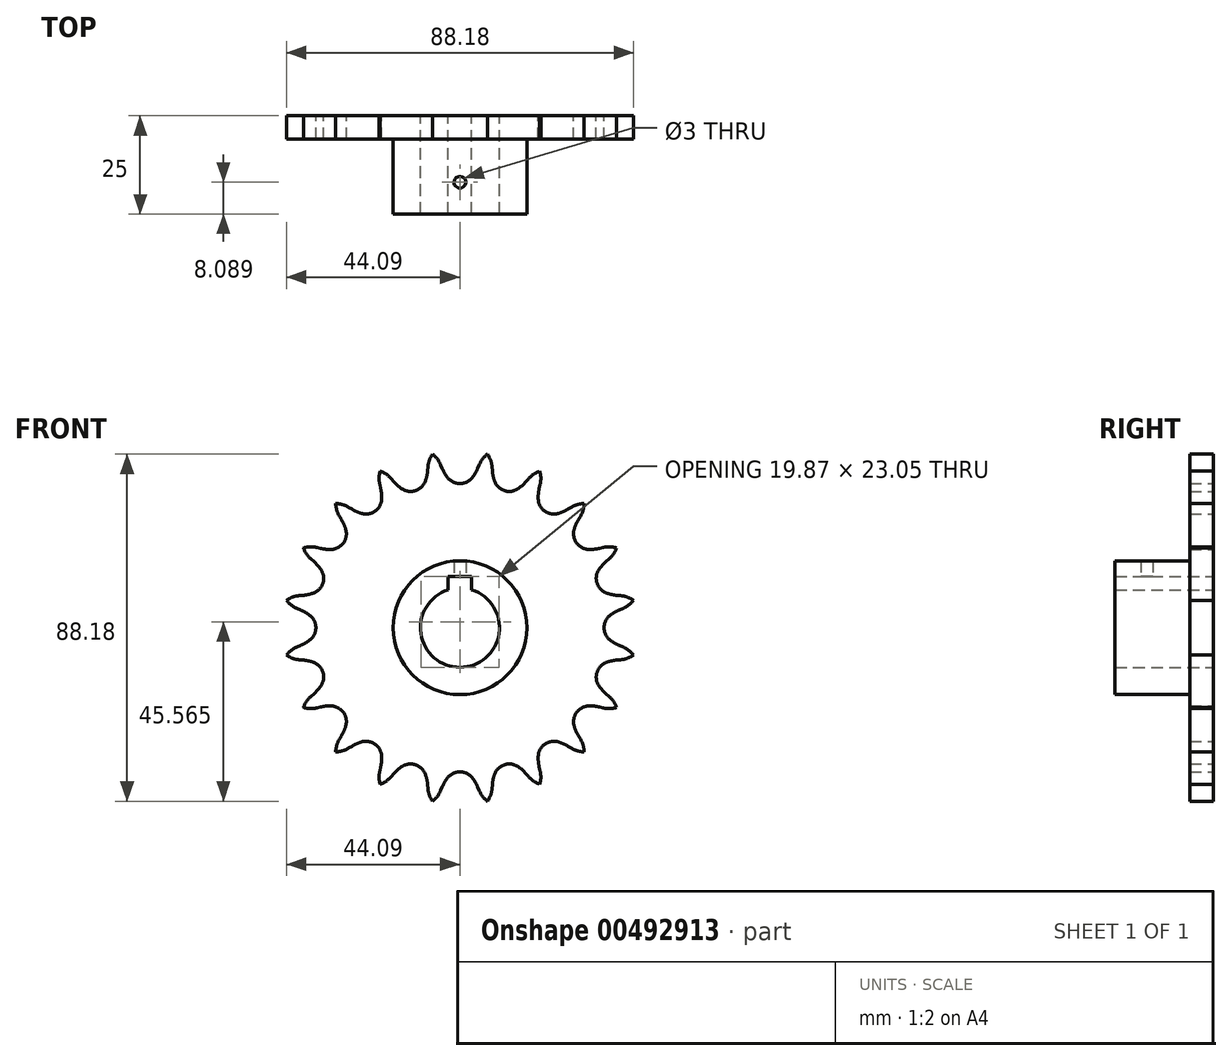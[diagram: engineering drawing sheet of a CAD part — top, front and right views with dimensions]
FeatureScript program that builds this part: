
annotation { "Feature Type Name" : "Feature", "Feature Type Description" : "" }
export const myFeature = defineFeature(function(context is Context, id is Id, definition is map)
    precondition{}
    {
        {
            var Q0;
            Q0=qCreatedBy(makeId("Front.planeOp"),FACE);
            var sketch = newSketch(context, id + "F0", { "sketchPlane" : qUnion([Q0])});
            skCircle(sketch, "E0", {"center": v(0, 0) * mm, "radius": 40.6 * mm, "construction": true});
            skLineSegment(sketch, "E1", {"start": v(0, 0) * mm, "end": v(0, 68.21) * mm, "construction": true});
            skLineSegment(sketch, "E2", {"start": v(-42.58, 40.6) * mm, "end": v(46.68, 40.6) * mm, "construction": true});
            skArc(sketch, "E3", {"start": v(-3.14, 38.14) * mm, "mid": v(-1.75, 37.01) * mm, "end": v(0, 36.61) * mm});
            skLineSegment(sketch, "E4.0", {"start": v(5, 0) * mm, "end": v(5, 68.21) * mm, "construction": true});
            skLineSegment(sketch, "E5.0", {"start": v(-42.58, 44.5) * mm, "end": v(46.68, 44.5) * mm, "construction": true});
            skLineSegment(sketch, "E6", {"start": v(-5.48, 36.31) * mm, "end": v(8.35, 47.12) * mm, "construction": true});
            skLineSegment(sketch, "E7", {"start": v(5, 44.5) * mm, "end": v(-4.52, 40.5) * mm, "construction": true});
            skArc(sketch, "E8", {"start": v(-4.52, 40.5) * mm, "mid": v(-3.9, 39.27) * mm, "end": v(-3.14, 38.14) * mm});
            skLineSegment(sketch, "E9", {"start": v(-4.52, 40.5) * mm, "end": v(-4.9, 41.4) * mm});
            skLineSegment(sketch, "E10.0", {"start": v(-10.95, 0) * mm, "end": v(-10.95, 68.21) * mm, "construction": true});
            skLineSegment(sketch, "E11.0", {"start": v(-42.58, 38.86) * mm, "end": v(46.68, 38.86) * mm, "construction": true});
            skLineSegment(sketch, "E12", {"start": v(0, 0) * mm, "end": v(-9.3, 58.75) * mm, "construction": true});
            skArc(sketch, "E13.trimOffspring", {"start": v(-4.89, 41.37) * mm, "mid": v(-5.75, 42.87) * mm, "end": v(-6.98, 44.09) * mm});
            skArc(sketch, "E14.trimOffspring", {"start": v(3.98, 40.4) * mm, "mid": v(3.98, 40.5) * mm, "end": v(3.98, 40.6) * mm});
            skArc(sketch, "E15.MirrorCS", {"start": v(4.89, 41.37) * mm, "mid": v(5.75, 42.87) * mm, "end": v(6.98, 44.09) * mm});
            skLineSegment(sketch, "E16.MirrorCS", {"start": v(4.52, 40.5) * mm, "end": v(4.9, 41.4) * mm});
            skArc(sketch, "E17.MirrorCS", {"start": v(4.52, 40.5) * mm, "mid": v(3.9, 39.27) * mm, "end": v(3.14, 38.14) * mm});
            skArc(sketch, "E18.MirrorCS", {"start": v(3.14, 38.14) * mm, "mid": v(1.75, 37.01) * mm, "end": v(0, 36.61) * mm});
            skArc(sketch, "E19.1.0", {"start": v(-17.43, 37.84) * mm, "mid": v(-18.72, 39) * mm, "end": v(-20.26, 39.77) * mm});
            skLineSegment(sketch, "E19.1.1", {"start": v(-16.81, 37.12) * mm, "end": v(-17.45, 37.86) * mm});
            skArc(sketch, "E19.1.2", {"start": v(-16.81, 37.12) * mm, "mid": v(-15.85, 36.14) * mm, "end": v(-14.77, 35.3) * mm});
            skArc(sketch, "E19.1.3", {"start": v(-14.77, 35.3) * mm, "mid": v(-13.1, 34.66) * mm, "end": v(-11.31, 34.82) * mm});
            skArc(sketch, "E19.1.4", {"start": v(-8.8, 37.24) * mm, "mid": v(-9.78, 35.74) * mm, "end": v(-11.31, 34.82) * mm});
            skArc(sketch, "E19.1.5", {"start": v(-8.22, 39.9) * mm, "mid": v(-8.42, 38.56) * mm, "end": v(-8.8, 37.24) * mm});
            skLineSegment(sketch, "E19.1.6", {"start": v(-8.22, 39.9) * mm, "end": v(-8.13, 40.89) * mm});
            skArc(sketch, "E19.1.7", {"start": v(-8.14, 40.86) * mm, "mid": v(-7.77, 42.55) * mm, "end": v(-6.98, 44.09) * mm});
            skArc(sketch, "E19.2.0", {"start": v(-28.27, 30.6) * mm, "mid": v(-29.85, 31.3) * mm, "end": v(-31.56, 31.56) * mm});
            skLineSegment(sketch, "E19.2.1", {"start": v(-27.46, 30.1) * mm, "end": v(-28.3, 30.61) * mm});
            skArc(sketch, "E19.2.2", {"start": v(-27.46, 30.1) * mm, "mid": v(-26.24, 29.48) * mm, "end": v(-24.96, 29.01) * mm});
            skArc(sketch, "E19.2.3", {"start": v(-24.96, 29.01) * mm, "mid": v(-23.17, 28.92) * mm, "end": v(-21.52, 29.62) * mm});
            skArc(sketch, "E19.2.4", {"start": v(-19.88, 32.7) * mm, "mid": v(-20.34, 30.97) * mm, "end": v(-21.52, 29.62) * mm});
            skArc(sketch, "E19.2.5", {"start": v(-20.15, 35.42) * mm, "mid": v(-19.92, 34.07) * mm, "end": v(-19.88, 32.7) * mm});
            skLineSegment(sketch, "E19.2.6", {"start": v(-20.15, 35.42) * mm, "end": v(-20.37, 36.37) * mm});
            skArc(sketch, "E19.2.7", {"start": v(-20.36, 36.34) * mm, "mid": v(-20.54, 38.06) * mm, "end": v(-20.26, 39.77) * mm});
            skArc(sketch, "E20.1.3.0", {"start": v(-36.34, 20.36) * mm, "mid": v(-38.06, 20.54) * mm, "end": v(-39.77, 20.26) * mm});
            skLineSegment(sketch, "E20.4.3.0", {"start": v(-35.42, 20.15) * mm, "end": v(-36.37, 20.37) * mm});
            skArc(sketch, "E20.7.3.0", {"start": v(-35.42, 20.15) * mm, "mid": v(-34.07, 19.92) * mm, "end": v(-32.7, 19.88) * mm});
            skArc(sketch, "E20.11.3.0", {"start": v(-32.7, 19.88) * mm, "mid": v(-30.97, 20.34) * mm, "end": v(-29.62, 21.52) * mm});
            skArc(sketch, "E20.15.3.0", {"start": v(-29.01, 24.96) * mm, "mid": v(-28.92, 23.17) * mm, "end": v(-29.62, 21.52) * mm});
            skArc(sketch, "E20.19.3.0", {"start": v(-30.1, 27.46) * mm, "mid": v(-29.48, 26.24) * mm, "end": v(-29.01, 24.96) * mm});
            skLineSegment(sketch, "E20.23.3.0", {"start": v(-30.1, 27.46) * mm, "end": v(-30.61, 28.3) * mm});
            skArc(sketch, "E20.26.3.0", {"start": v(-30.6, 28.27) * mm, "mid": v(-31.3, 29.85) * mm, "end": v(-31.56, 31.56) * mm});
            skArc(sketch, "E20.1.4.0", {"start": v(-40.86, 8.14) * mm, "mid": v(-42.55, 7.77) * mm, "end": v(-44.09, 6.98) * mm});
            skLineSegment(sketch, "E20.4.4.0", {"start": v(-39.9, 8.22) * mm, "end": v(-40.89, 8.13) * mm});
            skArc(sketch, "E20.7.4.0", {"start": v(-39.9, 8.22) * mm, "mid": v(-38.56, 8.42) * mm, "end": v(-37.24, 8.8) * mm});
            skArc(sketch, "E20.11.4.0", {"start": v(-37.24, 8.8) * mm, "mid": v(-35.74, 9.78) * mm, "end": v(-34.82, 11.31) * mm});
            skArc(sketch, "E20.15.4.0", {"start": v(-35.3, 14.77) * mm, "mid": v(-34.66, 13.1) * mm, "end": v(-34.82, 11.31) * mm});
            skArc(sketch, "E20.19.4.0", {"start": v(-37.12, 16.81) * mm, "mid": v(-36.14, 15.85) * mm, "end": v(-35.3, 14.77) * mm});
            skLineSegment(sketch, "E20.23.4.0", {"start": v(-37.12, 16.81) * mm, "end": v(-37.86, 17.45) * mm});
            skArc(sketch, "E20.26.4.0", {"start": v(-37.84, 17.43) * mm, "mid": v(-39, 18.72) * mm, "end": v(-39.77, 20.26) * mm});
            skArc(sketch, "E20.1.5.0", {"start": v(-41.37, -4.89) * mm, "mid": v(-42.87, -5.75) * mm, "end": v(-44.09, -6.98) * mm});
            skLineSegment(sketch, "E20.4.5.0", {"start": v(-40.5, -4.52) * mm, "end": v(-41.4, -4.9) * mm});
            skArc(sketch, "E20.7.5.0", {"start": v(-40.5, -4.52) * mm, "mid": v(-39.27, -3.9) * mm, "end": v(-38.14, -3.14) * mm});
            skArc(sketch, "E20.11.5.0", {"start": v(-38.14, -3.14) * mm, "mid": v(-37.01, -1.75) * mm, "end": v(-36.61, 0) * mm});
            skArc(sketch, "E20.15.5.0", {"start": v(-38.14, 3.14) * mm, "mid": v(-37.01, 1.75) * mm, "end": v(-36.61, 0) * mm});
            skArc(sketch, "E20.19.5.0", {"start": v(-40.5, 4.52) * mm, "mid": v(-39.27, 3.9) * mm, "end": v(-38.14, 3.14) * mm});
            skLineSegment(sketch, "E20.23.5.0", {"start": v(-40.5, 4.52) * mm, "end": v(-41.4, 4.9) * mm});
            skArc(sketch, "E20.26.5.0", {"start": v(-41.37, 4.89) * mm, "mid": v(-42.87, 5.75) * mm, "end": v(-44.09, 6.98) * mm});
            skArc(sketch, "E20.1.6.0", {"start": v(-37.84, -17.43) * mm, "mid": v(-39, -18.72) * mm, "end": v(-39.77, -20.26) * mm});
            skLineSegment(sketch, "E20.4.6.0", {"start": v(-37.12, -16.81) * mm, "end": v(-37.86, -17.45) * mm});
            skArc(sketch, "E20.7.6.0", {"start": v(-37.12, -16.81) * mm, "mid": v(-36.14, -15.85) * mm, "end": v(-35.3, -14.77) * mm});
            skArc(sketch, "E20.11.6.0", {"start": v(-35.3, -14.77) * mm, "mid": v(-34.66, -13.1) * mm, "end": v(-34.82, -11.31) * mm});
            skArc(sketch, "E20.15.6.0", {"start": v(-37.24, -8.8) * mm, "mid": v(-35.74, -9.78) * mm, "end": v(-34.82, -11.31) * mm});
            skArc(sketch, "E20.19.6.0", {"start": v(-39.9, -8.22) * mm, "mid": v(-38.56, -8.42) * mm, "end": v(-37.24, -8.8) * mm});
            skLineSegment(sketch, "E20.23.6.0", {"start": v(-39.9, -8.22) * mm, "end": v(-40.89, -8.13) * mm});
            skArc(sketch, "E20.26.6.0", {"start": v(-40.86, -8.14) * mm, "mid": v(-42.55, -7.77) * mm, "end": v(-44.09, -6.98) * mm});
            skArc(sketch, "E20.1.7.0", {"start": v(-30.6, -28.27) * mm, "mid": v(-31.3, -29.85) * mm, "end": v(-31.56, -31.56) * mm});
            skLineSegment(sketch, "E20.4.7.0", {"start": v(-30.1, -27.46) * mm, "end": v(-30.61, -28.3) * mm});
            skArc(sketch, "E20.7.7.0", {"start": v(-30.1, -27.46) * mm, "mid": v(-29.48, -26.24) * mm, "end": v(-29.01, -24.96) * mm});
            skArc(sketch, "E20.11.7.0", {"start": v(-29.01, -24.96) * mm, "mid": v(-28.92, -23.17) * mm, "end": v(-29.62, -21.52) * mm});
            skArc(sketch, "E20.15.7.0", {"start": v(-32.7, -19.88) * mm, "mid": v(-30.97, -20.34) * mm, "end": v(-29.62, -21.52) * mm});
            skArc(sketch, "E20.19.7.0", {"start": v(-35.42, -20.15) * mm, "mid": v(-34.07, -19.92) * mm, "end": v(-32.7, -19.88) * mm});
            skLineSegment(sketch, "E20.23.7.0", {"start": v(-35.42, -20.15) * mm, "end": v(-36.37, -20.37) * mm});
            skArc(sketch, "E20.26.7.0", {"start": v(-36.34, -20.36) * mm, "mid": v(-38.06, -20.54) * mm, "end": v(-39.77, -20.26) * mm});
            skArc(sketch, "E20.1.8.0", {"start": v(-20.36, -36.34) * mm, "mid": v(-20.54, -38.06) * mm, "end": v(-20.26, -39.77) * mm});
            skLineSegment(sketch, "E20.4.8.0", {"start": v(-20.15, -35.42) * mm, "end": v(-20.37, -36.37) * mm});
            skArc(sketch, "E20.7.8.0", {"start": v(-20.15, -35.42) * mm, "mid": v(-19.92, -34.07) * mm, "end": v(-19.88, -32.7) * mm});
            skArc(sketch, "E20.11.8.0", {"start": v(-19.88, -32.7) * mm, "mid": v(-20.34, -30.97) * mm, "end": v(-21.52, -29.62) * mm});
            skArc(sketch, "E20.15.8.0", {"start": v(-24.96, -29.01) * mm, "mid": v(-23.17, -28.92) * mm, "end": v(-21.52, -29.62) * mm});
            skArc(sketch, "E20.19.8.0", {"start": v(-27.46, -30.1) * mm, "mid": v(-26.24, -29.48) * mm, "end": v(-24.96, -29.01) * mm});
            skLineSegment(sketch, "E20.23.8.0", {"start": v(-27.46, -30.1) * mm, "end": v(-28.3, -30.61) * mm});
            skArc(sketch, "E20.26.8.0", {"start": v(-28.27, -30.6) * mm, "mid": v(-29.85, -31.3) * mm, "end": v(-31.56, -31.56) * mm});
            skArc(sketch, "E20.1.9.0", {"start": v(-8.14, -40.86) * mm, "mid": v(-7.77, -42.55) * mm, "end": v(-6.98, -44.09) * mm});
            skLineSegment(sketch, "E20.4.9.0", {"start": v(-8.22, -39.9) * mm, "end": v(-8.13, -40.89) * mm});
            skArc(sketch, "E20.7.9.0", {"start": v(-8.22, -39.9) * mm, "mid": v(-8.42, -38.56) * mm, "end": v(-8.8, -37.24) * mm});
            skArc(sketch, "E20.11.9.0", {"start": v(-8.8, -37.24) * mm, "mid": v(-9.78, -35.74) * mm, "end": v(-11.31, -34.82) * mm});
            skArc(sketch, "E20.15.9.0", {"start": v(-14.77, -35.3) * mm, "mid": v(-13.1, -34.66) * mm, "end": v(-11.31, -34.82) * mm});
            skArc(sketch, "E20.19.9.0", {"start": v(-16.81, -37.12) * mm, "mid": v(-15.85, -36.14) * mm, "end": v(-14.77, -35.3) * mm});
            skLineSegment(sketch, "E20.23.9.0", {"start": v(-16.81, -37.12) * mm, "end": v(-17.45, -37.86) * mm});
            skArc(sketch, "E20.26.9.0", {"start": v(-17.43, -37.84) * mm, "mid": v(-18.72, -39) * mm, "end": v(-20.26, -39.77) * mm});
            skArc(sketch, "E20.1.10.0", {"start": v(4.89, -41.37) * mm, "mid": v(5.75, -42.87) * mm, "end": v(6.98, -44.09) * mm});
            skLineSegment(sketch, "E20.4.10.0", {"start": v(4.52, -40.5) * mm, "end": v(4.9, -41.4) * mm});
            skArc(sketch, "E20.7.10.0", {"start": v(4.52, -40.5) * mm, "mid": v(3.9, -39.27) * mm, "end": v(3.14, -38.14) * mm});
            skArc(sketch, "E20.11.10.0", {"start": v(3.14, -38.14) * mm, "mid": v(1.75, -37.01) * mm, "end": v(0, -36.61) * mm});
            skArc(sketch, "E20.15.10.0", {"start": v(-3.14, -38.14) * mm, "mid": v(-1.75, -37.01) * mm, "end": v(0, -36.61) * mm});
            skArc(sketch, "E20.19.10.0", {"start": v(-4.52, -40.5) * mm, "mid": v(-3.9, -39.27) * mm, "end": v(-3.14, -38.14) * mm});
            skLineSegment(sketch, "E20.23.10.0", {"start": v(-4.52, -40.5) * mm, "end": v(-4.9, -41.4) * mm});
            skArc(sketch, "E20.26.10.0", {"start": v(-4.89, -41.37) * mm, "mid": v(-5.75, -42.87) * mm, "end": v(-6.98, -44.09) * mm});
            skArc(sketch, "E20.1.11.0", {"start": v(17.43, -37.84) * mm, "mid": v(18.72, -39) * mm, "end": v(20.26, -39.77) * mm});
            skLineSegment(sketch, "E20.4.11.0", {"start": v(16.81, -37.12) * mm, "end": v(17.45, -37.86) * mm});
            skArc(sketch, "E20.7.11.0", {"start": v(16.81, -37.12) * mm, "mid": v(15.85, -36.14) * mm, "end": v(14.77, -35.3) * mm});
            skArc(sketch, "E20.11.11.0", {"start": v(14.77, -35.3) * mm, "mid": v(13.1, -34.66) * mm, "end": v(11.31, -34.82) * mm});
            skArc(sketch, "E20.15.11.0", {"start": v(8.8, -37.24) * mm, "mid": v(9.78, -35.74) * mm, "end": v(11.31, -34.82) * mm});
            skArc(sketch, "E20.19.11.0", {"start": v(8.22, -39.9) * mm, "mid": v(8.42, -38.56) * mm, "end": v(8.8, -37.24) * mm});
            skLineSegment(sketch, "E20.23.11.0", {"start": v(8.22, -39.9) * mm, "end": v(8.13, -40.89) * mm});
            skArc(sketch, "E20.26.11.0", {"start": v(8.14, -40.86) * mm, "mid": v(7.77, -42.55) * mm, "end": v(6.98, -44.09) * mm});
            skArc(sketch, "E20.1.12.0", {"start": v(28.27, -30.6) * mm, "mid": v(29.85, -31.3) * mm, "end": v(31.56, -31.56) * mm});
            skLineSegment(sketch, "E20.4.12.0", {"start": v(27.46, -30.1) * mm, "end": v(28.3, -30.61) * mm});
            skArc(sketch, "E20.7.12.0", {"start": v(27.46, -30.1) * mm, "mid": v(26.24, -29.48) * mm, "end": v(24.96, -29.01) * mm});
            skArc(sketch, "E20.11.12.0", {"start": v(24.96, -29.01) * mm, "mid": v(23.17, -28.92) * mm, "end": v(21.52, -29.62) * mm});
            skArc(sketch, "E20.15.12.0", {"start": v(19.88, -32.7) * mm, "mid": v(20.34, -30.97) * mm, "end": v(21.52, -29.62) * mm});
            skArc(sketch, "E20.19.12.0", {"start": v(20.15, -35.42) * mm, "mid": v(19.92, -34.07) * mm, "end": v(19.88, -32.7) * mm});
            skLineSegment(sketch, "E20.23.12.0", {"start": v(20.15, -35.42) * mm, "end": v(20.37, -36.37) * mm});
            skArc(sketch, "E20.26.12.0", {"start": v(20.36, -36.34) * mm, "mid": v(20.54, -38.06) * mm, "end": v(20.26, -39.77) * mm});
            skArc(sketch, "E20.1.13.0", {"start": v(36.34, -20.36) * mm, "mid": v(38.06, -20.54) * mm, "end": v(39.77, -20.26) * mm});
            skLineSegment(sketch, "E20.4.13.0", {"start": v(35.42, -20.15) * mm, "end": v(36.37, -20.37) * mm});
            skArc(sketch, "E20.7.13.0", {"start": v(35.42, -20.15) * mm, "mid": v(34.07, -19.92) * mm, "end": v(32.7, -19.88) * mm});
            skArc(sketch, "E20.11.13.0", {"start": v(32.7, -19.88) * mm, "mid": v(30.97, -20.34) * mm, "end": v(29.62, -21.52) * mm});
            skArc(sketch, "E20.15.13.0", {"start": v(29.01, -24.96) * mm, "mid": v(28.92, -23.17) * mm, "end": v(29.62, -21.52) * mm});
            skArc(sketch, "E20.19.13.0", {"start": v(30.1, -27.46) * mm, "mid": v(29.48, -26.24) * mm, "end": v(29.01, -24.96) * mm});
            skLineSegment(sketch, "E20.23.13.0", {"start": v(30.1, -27.46) * mm, "end": v(30.61, -28.3) * mm});
            skArc(sketch, "E20.26.13.0", {"start": v(30.6, -28.27) * mm, "mid": v(31.3, -29.85) * mm, "end": v(31.56, -31.56) * mm});
            skArc(sketch, "E20.1.14.0", {"start": v(40.86, -8.14) * mm, "mid": v(42.55, -7.77) * mm, "end": v(44.09, -6.98) * mm});
            skLineSegment(sketch, "E20.4.14.0", {"start": v(39.9, -8.22) * mm, "end": v(40.89, -8.13) * mm});
            skArc(sketch, "E20.7.14.0", {"start": v(39.9, -8.22) * mm, "mid": v(38.56, -8.42) * mm, "end": v(37.24, -8.8) * mm});
            skArc(sketch, "E20.11.14.0", {"start": v(37.24, -8.8) * mm, "mid": v(35.74, -9.78) * mm, "end": v(34.82, -11.31) * mm});
            skArc(sketch, "E20.15.14.0", {"start": v(35.3, -14.77) * mm, "mid": v(34.66, -13.1) * mm, "end": v(34.82, -11.31) * mm});
            skArc(sketch, "E20.19.14.0", {"start": v(37.12, -16.81) * mm, "mid": v(36.14, -15.85) * mm, "end": v(35.3, -14.77) * mm});
            skLineSegment(sketch, "E20.23.14.0", {"start": v(37.12, -16.81) * mm, "end": v(37.86, -17.45) * mm});
            skArc(sketch, "E20.26.14.0", {"start": v(37.84, -17.43) * mm, "mid": v(39, -18.72) * mm, "end": v(39.77, -20.26) * mm});
            skArc(sketch, "E20.1.15.0", {"start": v(41.37, 4.89) * mm, "mid": v(42.87, 5.75) * mm, "end": v(44.09, 6.98) * mm});
            skLineSegment(sketch, "E20.4.15.0", {"start": v(40.5, 4.52) * mm, "end": v(41.4, 4.9) * mm});
            skArc(sketch, "E20.7.15.0", {"start": v(40.5, 4.52) * mm, "mid": v(39.27, 3.9) * mm, "end": v(38.14, 3.14) * mm});
            skArc(sketch, "E20.11.15.0", {"start": v(38.14, 3.14) * mm, "mid": v(37.01, 1.75) * mm, "end": v(36.61, 0) * mm});
            skArc(sketch, "E20.15.15.0", {"start": v(38.14, -3.14) * mm, "mid": v(37.01, -1.75) * mm, "end": v(36.61, 0) * mm});
            skArc(sketch, "E20.19.15.0", {"start": v(40.5, -4.52) * mm, "mid": v(39.27, -3.9) * mm, "end": v(38.14, -3.14) * mm});
            skLineSegment(sketch, "E20.23.15.0", {"start": v(40.5, -4.52) * mm, "end": v(41.4, -4.9) * mm});
            skArc(sketch, "E20.26.15.0", {"start": v(41.37, -4.89) * mm, "mid": v(42.87, -5.75) * mm, "end": v(44.09, -6.98) * mm});
            skArc(sketch, "E20.1.16.0", {"start": v(37.84, 17.43) * mm, "mid": v(39, 18.72) * mm, "end": v(39.77, 20.26) * mm});
            skLineSegment(sketch, "E20.4.16.0", {"start": v(37.12, 16.81) * mm, "end": v(37.86, 17.45) * mm});
            skArc(sketch, "E20.7.16.0", {"start": v(37.12, 16.81) * mm, "mid": v(36.14, 15.85) * mm, "end": v(35.3, 14.77) * mm});
            skArc(sketch, "E20.11.16.0", {"start": v(35.3, 14.77) * mm, "mid": v(34.66, 13.1) * mm, "end": v(34.82, 11.31) * mm});
            skArc(sketch, "E20.15.16.0", {"start": v(37.24, 8.8) * mm, "mid": v(35.74, 9.78) * mm, "end": v(34.82, 11.31) * mm});
            skArc(sketch, "E20.19.16.0", {"start": v(39.9, 8.22) * mm, "mid": v(38.56, 8.42) * mm, "end": v(37.24, 8.8) * mm});
            skLineSegment(sketch, "E20.23.16.0", {"start": v(39.9, 8.22) * mm, "end": v(40.89, 8.13) * mm});
            skArc(sketch, "E20.26.16.0", {"start": v(40.86, 8.14) * mm, "mid": v(42.55, 7.77) * mm, "end": v(44.09, 6.98) * mm});
            skArc(sketch, "E20.1.17.0", {"start": v(30.6, 28.27) * mm, "mid": v(31.3, 29.85) * mm, "end": v(31.56, 31.56) * mm});
            skLineSegment(sketch, "E20.4.17.0", {"start": v(30.1, 27.46) * mm, "end": v(30.61, 28.3) * mm});
            skArc(sketch, "E20.7.17.0", {"start": v(30.1, 27.46) * mm, "mid": v(29.48, 26.24) * mm, "end": v(29.01, 24.96) * mm});
            skArc(sketch, "E20.11.17.0", {"start": v(29.01, 24.96) * mm, "mid": v(28.92, 23.17) * mm, "end": v(29.62, 21.52) * mm});
            skArc(sketch, "E20.15.17.0", {"start": v(32.7, 19.88) * mm, "mid": v(30.97, 20.34) * mm, "end": v(29.62, 21.52) * mm});
            skArc(sketch, "E20.19.17.0", {"start": v(35.42, 20.15) * mm, "mid": v(34.07, 19.92) * mm, "end": v(32.7, 19.88) * mm});
            skLineSegment(sketch, "E20.23.17.0", {"start": v(35.42, 20.15) * mm, "end": v(36.37, 20.37) * mm});
            skArc(sketch, "E20.26.17.0", {"start": v(36.34, 20.36) * mm, "mid": v(38.06, 20.54) * mm, "end": v(39.77, 20.26) * mm});
            skArc(sketch, "E20.1.18.0", {"start": v(20.36, 36.34) * mm, "mid": v(20.54, 38.06) * mm, "end": v(20.26, 39.77) * mm});
            skLineSegment(sketch, "E20.4.18.0", {"start": v(20.15, 35.42) * mm, "end": v(20.37, 36.37) * mm});
            skArc(sketch, "E20.7.18.0", {"start": v(20.15, 35.42) * mm, "mid": v(19.92, 34.07) * mm, "end": v(19.88, 32.7) * mm});
            skArc(sketch, "E20.11.18.0", {"start": v(19.88, 32.7) * mm, "mid": v(20.34, 30.97) * mm, "end": v(21.52, 29.62) * mm});
            skArc(sketch, "E20.15.18.0", {"start": v(24.96, 29.01) * mm, "mid": v(23.17, 28.92) * mm, "end": v(21.52, 29.62) * mm});
            skArc(sketch, "E20.19.18.0", {"start": v(27.46, 30.1) * mm, "mid": v(26.24, 29.48) * mm, "end": v(24.96, 29.01) * mm});
            skLineSegment(sketch, "E20.23.18.0", {"start": v(27.46, 30.1) * mm, "end": v(28.3, 30.61) * mm});
            skArc(sketch, "E20.26.18.0", {"start": v(28.27, 30.6) * mm, "mid": v(29.85, 31.3) * mm, "end": v(31.56, 31.56) * mm});
            skArc(sketch, "E20.1.19.0", {"start": v(8.14, 40.86) * mm, "mid": v(7.77, 42.55) * mm, "end": v(6.98, 44.09) * mm});
            skLineSegment(sketch, "E20.4.19.0", {"start": v(8.22, 39.9) * mm, "end": v(8.13, 40.89) * mm});
            skArc(sketch, "E20.7.19.0", {"start": v(8.22, 39.9) * mm, "mid": v(8.42, 38.56) * mm, "end": v(8.8, 37.24) * mm});
            skArc(sketch, "E20.11.19.0", {"start": v(8.8, 37.24) * mm, "mid": v(9.78, 35.74) * mm, "end": v(11.31, 34.82) * mm});
            skArc(sketch, "E20.15.19.0", {"start": v(14.77, 35.3) * mm, "mid": v(13.1, 34.66) * mm, "end": v(11.31, 34.82) * mm});
            skArc(sketch, "E20.19.19.0", {"start": v(16.81, 37.12) * mm, "mid": v(15.85, 36.14) * mm, "end": v(14.77, 35.3) * mm});
            skLineSegment(sketch, "E20.23.19.0", {"start": v(16.81, 37.12) * mm, "end": v(17.45, 37.86) * mm});
            skArc(sketch, "E20.26.19.0", {"start": v(17.43, 37.84) * mm, "mid": v(18.72, 39) * mm, "end": v(20.26, 39.77) * mm});
            skCircle(sketch, "E21", {"center": v(0, 0) * mm, "radius": 17 * mm});
            skCircle(sketch, "E22", {"center": v(0, 0) * mm, "radius": 10.05 * mm});
            skLineSegment(sketch, "E23.bottom", {"start": v(-3, 13) * mm, "end": v(3, 13) * mm});
            skLineSegment(sketch, "E23.top", {"start": v(-3, 0) * mm, "end": v(3, 0) * mm});
            skLineSegment(sketch, "E23.left", {"start": v(-3, 13) * mm, "end": v(-3, 0) * mm});
            skLineSegment(sketch, "E23.right", {"start": v(3, 13) * mm, "end": v(3, 0) * mm});
            skSolve(sketch);
        }
        {
            var Q0;
            Q0=makeQuery(id+"F0.imprint","IMPRINT",FACE,{"disambiguationData":[TD([[makeQuery(id+"F0.imprint","IMPRINT",EDGE,{"derivedFrom":sQuery(id+"F0.wireOp",EDGE,"E3")}),-1.0]])]});
            var Q1;
            Q1=makeQuery(id+"F0.imprint","IMPRINT",FACE,{"disambiguationData":[TD([[makeQuery(id+"F0.imprint","IMPRINT",EDGE,{"derivedFrom":sQuery(id+"F0.wireOp",EDGE,"E21")}),1.0]])]});
            extrude(context, id + "F1", {"entities" : qUnion([Q0, Q1]), "depth" : 6 * mm, "offsetDistance" : 25 * mm});
        }
        {
            var Q0;
            Q0=makeQuery(id+"F0.imprint","IMPRINT",FACE,{"disambiguationData":[TD([[makeQuery(id+"F0.imprint","IMPRINT",EDGE,{"derivedFrom":sQuery(id+"F0.wireOp",EDGE,"E21")}),1.0]])]});
            extrude(context, id + "F2", {"entities" : qUnion([Q0]), "operationType" : NewBodyOperationType.ADD, "depth" : 25 * mm, "offsetDistance" : 25 * mm});
        }
        {
            var Q0;
            Q0=qCreatedBy(makeId("Top.planeOp"),FACE);
            var sketch = newSketch(context, id + "F3", { "sketchPlane" : qUnion([Q0])});
            skLineSegment(sketch, "E24", {"start": v(0, -25) * mm, "end": v(0, -16.91) * mm, "construction": true});
            skCircle(sketch, "E25", {"center": v(0, -16.91) * mm, "radius": 1.5 * mm});
            skSolve(sketch);
        }
        {
            var Q0;
            Q0 = qSketchRegion(id + "F3", true);
            extrude(context, id + "F4", {"entities" : qUnion([Q0]), "operationType" : NewBodyOperationType.REMOVE, "depth" : 25 * mm, "offsetDistance" : 25 * mm});
        }
    });
